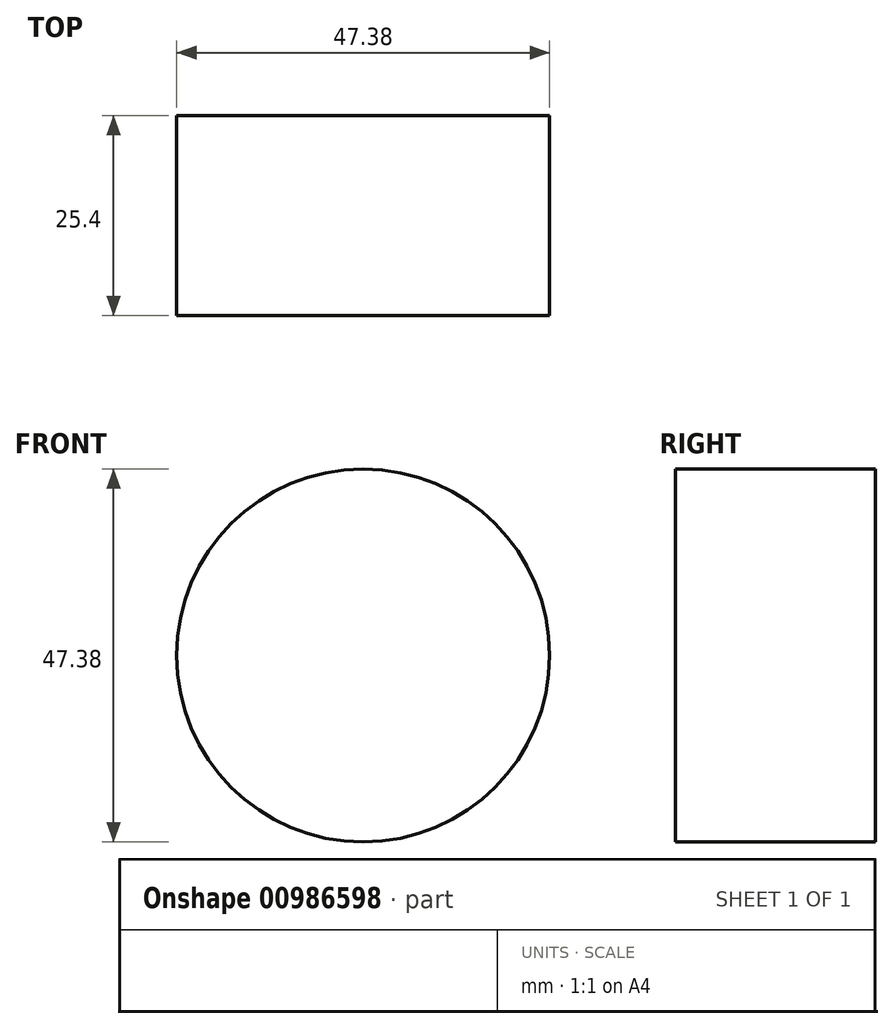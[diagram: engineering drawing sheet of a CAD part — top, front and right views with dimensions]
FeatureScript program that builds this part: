
annotation { "Feature Type Name" : "Feature", "Feature Type Description" : "" }
export const myFeature = defineFeature(function(context is Context, id is Id, definition is map)
    precondition{}
    {
        {
            var Q0;
            Q0=qCreatedBy(makeId("Front.planeOp"),FACE);
            var sketch = newSketch(context, id + "F0", { "sketchPlane" : qUnion([Q0])});
            skCircle(sketch, "E0", {"center": v(0, 0) * mm, "radius": 23.7 * mm});
            skSolve(sketch);
        }
        {
            var Q0;
            Q0=makeQuery(id+"F0.imprint","IMPRINT",FACE,{"disambiguationData":[TD([[makeQuery(id+"F0.imprint","IMPRINT",EDGE,{"derivedFrom":sQuery(id+"F0.wireOp",EDGE,"E0")}),1.0]])]});
            extrude(context, id + "F1", {"entities" : qUnion([Q0]), "depth" : 25.4 * mm, "offsetDistance" : 25.4 * mm});
        }
    });
